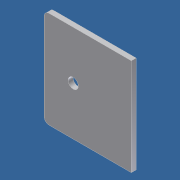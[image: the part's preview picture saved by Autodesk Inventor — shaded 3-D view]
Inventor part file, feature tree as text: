
AUTODESK INVENTOR PART (.ipt)
format: ipt  version: unknown  size: 172,544 bytes
history: native  units: in
note: dims shown in document units (in); Inventor stores cm internally (conversion verified against a paired STEP export)
features: extrude x1, fillet x1, hole x1, sketch x1
ambient origin geometry x8: Origin, YZ Plane, XZ Plane, XY Plane, X Axis, Y Axis, Z Axis, Center Point
bodies: Solid1 (feature_tree)
feature tree (4):
  extrude  "Extrusion1"  Depth=0.125in TaperAngle=0.0deg
  fillet  "Fillet1"  Radius=0.125in
  hole  "Hole1"  [1 undecoded]
  sketch  "Sketch1"  dims[d0=2.25in d1=0.125in d2=0.0in d3=0.125in d4=0.75in d5=1.25in d6=0.265in d7=0.75in d8=0.375in d9=0.25in d10=0.5635in d11=1.0in d12=0.8108in d13=2.5in]
note: 1 required parameter value undecoded (feature->parameter linkage not recoverable at this tier; creation-order binding heuristic only, values carry confidence <= 0.55)
